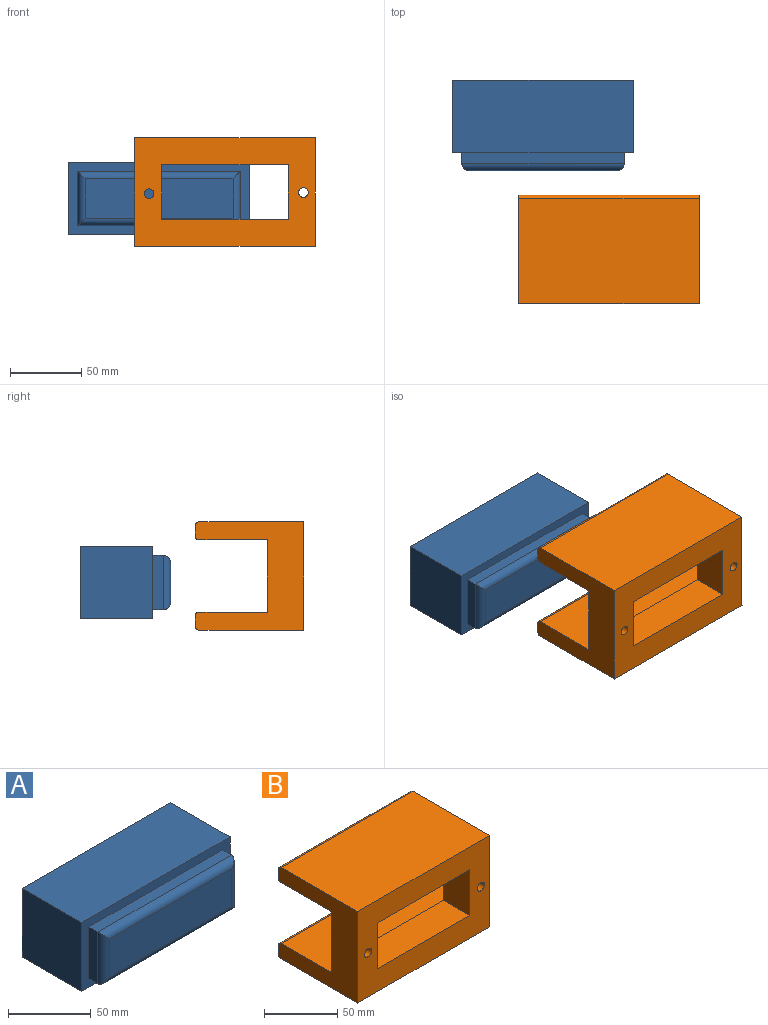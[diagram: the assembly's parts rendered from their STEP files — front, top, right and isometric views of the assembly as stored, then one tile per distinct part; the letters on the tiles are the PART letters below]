
ASSEMBLY  parts=2 mates=1
PART A: 15 faces, bbox 127x63.5x50.8 mm
  f0: plane 50.8x50.8mm, normal (-1,0,0), area 2580.6mm2, adj f1,f3,f4,f5
  f1: plane 127x50.8mm, normal (0,0,-1), area 6451.6mm2, adj f0,f2,f4,f5
  f2: plane 50.8x50.8mm, normal (1,0,0), area 2580.6mm2, adj f1,f3,f4,f5
  f3: plane 127x50.8mm, normal (0,0,1), area 6451.6mm2, adj f0,f2,f4,f5
  f4: plane 127x50.8mm, normal (0,-1,0), area 2096.8mm2, adj f0,f1,f2,f3,f6,f7,f8,f9
  f5: plane 127x50.8mm, normal (0,1,0), area 6451.6mm2, adj f0,f1,f2,f3
  f6: plane 114.3x7.62mm, normal (0,0,1), area 871mm2, adj f4,f7,f9,f11
  f7: plane 38.1x7.62mm, normal (-1,0,0), area 290.3mm2, adj f4,f6,f8,f12
  f8: plane 114.3x7.62mm, normal (0,0,-1), area 871mm2, adj f4,f7,f9,f14
  f9: plane 38.1x7.62mm, normal (1,0,0), area 290.3mm2, adj f4,f6,f8,f13
  f10: plane 104.14x27.94mm, normal (0,-1,0), area 2909.7mm2, adj f11,f12,f13,f14
  f11: cylinder r=5.08mm len=114.3mm, axis (1,0,0), area 882.6mm2, adj f6,f10,f12,f13
  f12: cylinder r=5.08mm len=38.1mm, axis (0,0,1), area 274.6mm2, adj f7,f10,f11,f14
  f13: cylinder r=5.08mm len=38.1mm, axis (0,0,-1), area 274.6mm2, adj f9,f10,f11,f14
  f14: cylinder r=5.08mm len=114.3mm, axis (-1,0,0), area 882.6mm2, adj f8,f10,f12,f13
PART B: 20 faces, bbox 127x76.2x76.2 mm
  f0: plane 127x76.2mm, normal (0,-1,0), area 6218.6mm2, adj f1,f7,f8,f9,f14,f15,f16,f17
  f1: plane 127x73.66mm, normal (0,0,-1), area 9354.8mm2, adj f0,f8,f9,f10
  f2: plane 127x7.62mm, normal (0,1,0), area 967.7mm2, adj f8,f9,f10,f11
  f3: plane 127x48.26mm, normal (0,0,1), area 6129mm2, adj f4,f8,f9,f11
  f4: plane 127x50.8mm, normal (0,1,0), area 2992.8mm2, adj f3,f5,f8,f9,f14,f15,f16,f17
  f5: plane 127x48.26mm, normal (0,0,-1), area 6129mm2, adj f4,f8,f9,f12
  f6: plane 127x7.62mm, normal (0,1,0), area 967.7mm2, adj f8,f9,f12,f13
  f7: plane 127x73.66mm, normal (0,0,1), area 9354.8mm2, adj f0,f8,f9,f13
  f8: plane 76.2x76.2mm, normal (1,0,0), area 3220.3mm2, adj f0,f1,f2,f3,f4,f5,f6,f7
  f9: plane 76.2x76.2mm, normal (-1,0,0), area 3220.3mm2, adj f0,f1,f2,f3,f4,f5,f6,f7
  f10: cylinder r=2.54mm len=127mm, axis (-1,0,0), area 506.7mm2, adj f1,f2,f8,f9
  f11: cylinder r=2.54mm len=127mm, axis (-1,0,0), area 506.7mm2, adj f2,f3,f8,f9
  f12: cylinder r=2.54mm len=127mm, axis (-1,0,0), area 506.7mm2, adj f5,f6,f8,f9
  f13: cylinder r=2.54mm len=127mm, axis (-1,0,0), area 506.7mm2, adj f6,f7,f8,f9
  f14: plane 88.9x25.4mm, normal (0,0,-1), area 2258.1mm2, adj f0,f4,f15,f17
  f15: plane 38.1x25.4mm, normal (1,0,0), area 967.7mm2, adj f0,f4,f14,f16
  f16: plane 88.9x25.4mm, normal (0,0,1), area 2258.1mm2, adj f0,f4,f15,f17
  f17: plane 38.1x25.4mm, normal (-1,0,0), area 967.7mm2, adj f0,f4,f14,f16
  f18: cylinder r=3.38mm len=25.4mm, axis (0,1,0), area 539.1mm2, adj f0,f4
  f19: cylinder r=3.38mm len=25.4mm, axis (0,1,0), area 539.1mm2, adj f0,f4
PLACE A t=(-133.46,123.39,-46.36)mm
PLACE B t=(-87.05,-33.71,-54.46)mm
MATE parallel A.f2 <-> B.f8  axis (1,0,0) through (-6.46,97.99,-20.96)mm
